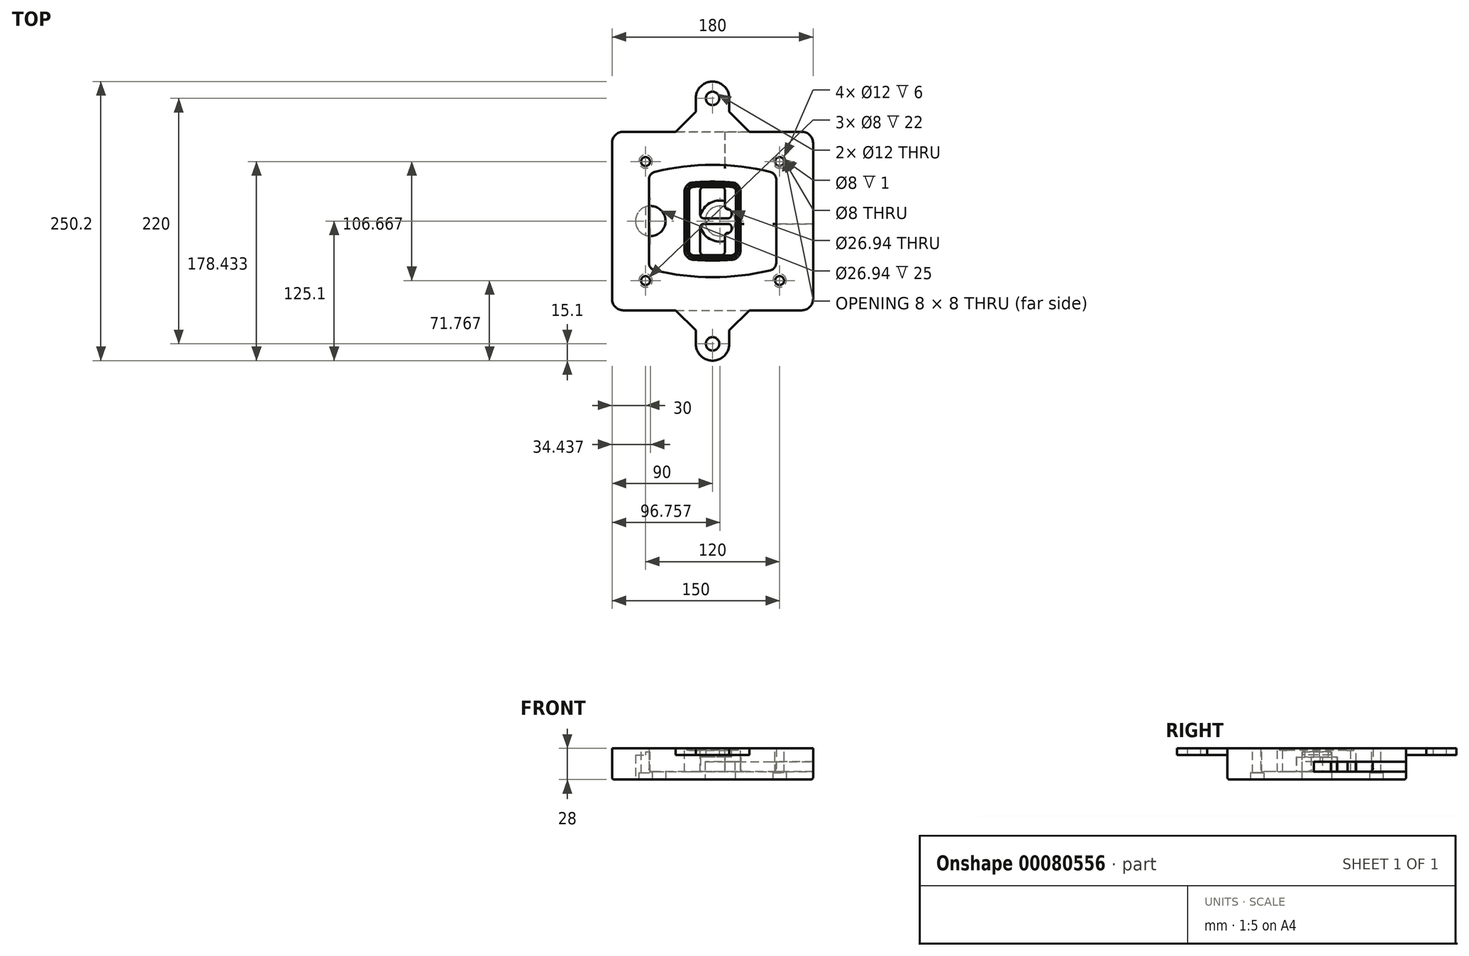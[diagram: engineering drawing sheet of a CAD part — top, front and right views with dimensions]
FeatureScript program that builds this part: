
annotation { "Feature Type Name" : "Feature", "Feature Type Description" : "" }
export const myFeature = defineFeature(function(context is Context, id is Id, definition is map)
    precondition{}
    {
        {
            var Q0;
            Q0=qCreatedBy(makeId("Top.planeOp"),FACE);
            var sketch = newSketch(context, id + "F0", { "sketchPlane" : qUnion([Q0])});
            skPoint(sketch, "E0.rect.middle", {"position": v(0, 0) * mm});
            skLineSegment(sketch, "E1.bottom", {"start": v(-80, -80) * mm, "end": v(80, -80) * mm});
            skLineSegment(sketch, "E1.top", {"start": v(-80, 80) * mm, "end": v(80, 80) * mm});
            skLineSegment(sketch, "E1.left", {"start": v(-90, -70) * mm, "end": v(-90, 70) * mm});
            skLineSegment(sketch, "E1.right", {"start": v(90, -70) * mm, "end": v(90, 70) * mm});
            skLineSegment(sketch, "E2", {"start": v(-90, 80) * mm, "end": v(90, -80) * mm, "construction": true});
            skLineSegment(sketch, "E3", {"start": v(90, 80) * mm, "end": v(-90, -80) * mm, "construction": true});
            skCircle(sketch, "E4", {"center": v(-60, 53.33) * mm, "radius": 4 * mm});
            skCircle(sketch, "E5", {"center": v(60, 53.33) * mm, "radius": 4 * mm});
            skCircle(sketch, "E6", {"center": v(60, -53.33) * mm, "radius": 4 * mm});
            skCircle(sketch, "E7", {"center": v(-60, -53.33) * mm, "radius": 4 * mm});
            skLineSegment(sketch, "E8", {"start": v(-60, 53.33) * mm, "end": v(60, 53.33) * mm, "construction": true});
            skLineSegment(sketch, "E9", {"start": v(60, 53.33) * mm, "end": v(60, -53.33) * mm, "construction": true});
            skLineSegment(sketch, "E10", {"start": v(60, -53.33) * mm, "end": v(-60, -53.33) * mm, "construction": true});
            skLineSegment(sketch, "E11", {"start": v(-60, -53.33) * mm, "end": v(-60, 53.33) * mm, "construction": true});
            skLineSegment(sketch, "E12", {"start": v(-60, 37.3) * mm, "end": v(-60, -37.3) * mm});
            skLineSegment(sketch, "E13", {"start": v(60, 37.3) * mm, "end": v(60, -37.3) * mm});
            skArc(sketch, "E14", {"start": v(52.38, 47.01) * mm, "mid": v(0, 53.33) * mm, "end": v(-52.38, 47.01) * mm});
            skArc(sketch, "E15", {"start": v(-52.38, -47.01) * mm, "mid": v(0, -53.33) * mm, "end": v(52.38, -47.01) * mm});
            skLineSegment(sketch, "E16", {"start": v(-60, 0) * mm, "end": v(60, 0) * mm, "construction": true});
            skPoint(sketch, "E17.visualSharp", {"position": v(-60, -45) * mm});
            skArc(sketch, "E17.filletArc", {"start": v(-60, -37.3) * mm, "mid": v(-57.87, -43.47) * mm, "end": v(-52.38, -47.01) * mm});
            skPoint(sketch, "E18.visualSharp", {"position": v(-60, 45) * mm});
            skArc(sketch, "E18.filletArc", {"start": v(-52.38, 47.01) * mm, "mid": v(-57.87, 43.47) * mm, "end": v(-60, 37.3) * mm});
            skPoint(sketch, "E19.visualSharp", {"position": v(60, 45) * mm});
            skArc(sketch, "E19.filletArc", {"start": v(60, 37.3) * mm, "mid": v(57.87, 43.47) * mm, "end": v(52.38, 47.01) * mm});
            skPoint(sketch, "E20.visualSharp", {"position": v(60, -45) * mm});
            skArc(sketch, "E20.filletArc", {"start": v(52.38, -47.01) * mm, "mid": v(57.87, -43.47) * mm, "end": v(60, -37.3) * mm});
            skPoint(sketch, "E21.visualSharp", {"position": v(-90, 80) * mm});
            skArc(sketch, "E21.filletArc", {"start": v(-80, 80) * mm, "mid": v(-87.07, 77.07) * mm, "end": v(-90, 70) * mm});
            skPoint(sketch, "E22.visualSharp", {"position": v(90, 80) * mm});
            skArc(sketch, "E22.filletArc", {"start": v(90, 70) * mm, "mid": v(87.07, 77.07) * mm, "end": v(80, 80) * mm});
            skPoint(sketch, "E23.visualSharp", {"position": v(90, -80) * mm});
            skArc(sketch, "E23.filletArc", {"start": v(80, -80) * mm, "mid": v(87.07, -77.07) * mm, "end": v(90, -70) * mm});
            skPoint(sketch, "E24.visualSharp", {"position": v(-90, -80) * mm});
            skArc(sketch, "E24.filletArc", {"start": v(-90, -70) * mm, "mid": v(-87.07, -77.07) * mm, "end": v(-80, -80) * mm});
            skArc(sketch, "E25.0", {"start": v(57, 37.3) * mm, "mid": v(55.5, 41.62) * mm, "end": v(51.67, 44.1) * mm});
            skLineSegment(sketch, "E25.1", {"start": v(57, 37.3) * mm, "end": v(57, -37.3) * mm});
            skArc(sketch, "E25.2", {"start": v(51.67, -44.1) * mm, "mid": v(55.5, -41.62) * mm, "end": v(57, -37.3) * mm});
            skArc(sketch, "E25.3", {"start": v(-51.67, -44.1) * mm, "mid": v(0, -50.33) * mm, "end": v(51.67, -44.1) * mm});
            skArc(sketch, "E25.4", {"start": v(-57, -37.3) * mm, "mid": v(-55.5, -41.62) * mm, "end": v(-51.67, -44.1) * mm});
            skArc(sketch, "E25.5", {"start": v(51.67, 44.1) * mm, "mid": v(0, 50.33) * mm, "end": v(-51.67, 44.1) * mm});
            skLineSegment(sketch, "E25.6", {"start": v(-57, 37.3) * mm, "end": v(-57, -37.3) * mm});
            skArc(sketch, "E25.7", {"start": v(-51.67, 44.1) * mm, "mid": v(-55.5, 41.62) * mm, "end": v(-57, 37.3) * mm});
            skArc(sketch, "E26.0", {"start": v(-53.33, 50.9) * mm, "mid": v(-61.01, 45.94) * mm, "end": v(-64, 37.3) * mm});
            skArc(sketch, "E26.1", {"start": v(53.33, 50.9) * mm, "mid": v(0, 57.33) * mm, "end": v(-53.33, 50.9) * mm});
            skArc(sketch, "E26.2", {"start": v(64, 37.3) * mm, "mid": v(61.01, 45.94) * mm, "end": v(53.33, 50.9) * mm});
            skLineSegment(sketch, "E26.3", {"start": v(64, 37.3) * mm, "end": v(64, -37.3) * mm});
            skArc(sketch, "E26.4", {"start": v(53.33, -50.9) * mm, "mid": v(61.01, -45.94) * mm, "end": v(64, -37.3) * mm});
            skLineSegment(sketch, "E26.5", {"start": v(-64, 37.3) * mm, "end": v(-64, -37.3) * mm});
            skArc(sketch, "E26.6", {"start": v(-53.33, -50.9) * mm, "mid": v(0, -57.33) * mm, "end": v(53.33, -50.9) * mm});
            skArc(sketch, "E26.7", {"start": v(-64, -37.3) * mm, "mid": v(-61.01, -45.94) * mm, "end": v(-53.33, -50.9) * mm});
            skSolve(sketch);
        }
        {
            var Q0;
            Q0=makeQuery(id+"F0.imprint","IMPRINT",FACE,{"disambiguationData":[TD([[makeQuery(id+"F0.imprint","IMPRINT",EDGE,{"derivedFrom":sQuery(id+"F0.wireOp",EDGE,"E1.bottom")}),1.0]])]});
            var Q1;
            Q1=makeQuery(id+"F0.imprint","IMPRINT",FACE,{"disambiguationData":[TD([[makeQuery(id+"F0.imprint","IMPRINT",EDGE,{"derivedFrom":sQuery(id+"F0.wireOp",EDGE,"E12")}),1.0]])]});
            var Q2;
            Q2=makeQuery(id+"F0.imprint","IMPRINT",FACE,{"disambiguationData":[TD([[makeQuery(id+"F0.imprint","IMPRINT",EDGE,{"derivedFrom":sQuery(id+"F0.wireOp",EDGE,"E25.0")}),1.0]])]});
            var Q3;
            Q3=makeQuery(id+"F0.imprint","IMPRINT",FACE,{"disambiguationData":[TD([[makeQuery(id+"F0.imprint","IMPRINT",EDGE,{"derivedFrom":sQuery(id+"F0.wireOp",EDGE,"E12")}),-1.0]])]});
            extrude(context, id + "F1", {"entities" : qUnion([Q0, Q1, Q2, Q3]), "oppositeDirection" : true, "depth" : 25 * mm});
        }
        {
            var Q0;
            Q0=makeQuery(id+"F0.imprint","IMPRINT",FACE,{"disambiguationData":[TD([[makeQuery(id+"F0.imprint","IMPRINT",EDGE,{"derivedFrom":sQuery(id+"F0.wireOp",EDGE,"E12")}),1.0]])]});
            extrude(context, id + "F2", {"entities" : qUnion([Q0]), "operationType" : NewBodyOperationType.ADD, "depth" : 3 * mm});
        }
        {
            var Q0;
            Q0=makeQuery(id+"F0.imprint","IMPRINT",FACE,{"disambiguationData":[TD([[makeQuery(id+"F0.imprint","IMPRINT",EDGE,{"derivedFrom":sQuery(id+"F0.wireOp",EDGE,"E25.0")}),1.0]])]});
            extrude(context, id + "F3", {"entities" : qUnion([Q0]), "operationType" : NewBodyOperationType.REMOVE, "oppositeDirection" : true, "depth" : 18 * mm});
        }
        {
            var Q0;
            Q0=makeQuery(id+"F2.opExtrude","CAP_FACE",FACE,{"disambiguationData":[OSD([sQuery(id+"F0.wireOp",EDGE,"E12"),sQuery(id+"F0.wireOp",EDGE,"E13"),sQuery(id+"F0.wireOp",EDGE,"E14"),sQuery(id+"F0.wireOp",EDGE,"E15"),sQuery(id+"F0.wireOp",EDGE,"E17.filletArc"),sQuery(id+"F0.wireOp",EDGE,"E18.filletArc"),sQuery(id+"F0.wireOp",EDGE,"E19.filletArc"),sQuery(id+"F0.wireOp",EDGE,"E20.filletArc"),sQuery(id+"F0.wireOp",EDGE,"E25.0"),sQuery(id+"F0.wireOp",EDGE,"E25.1"),sQuery(id+"F0.wireOp",EDGE,"E25.2"),sQuery(id+"F0.wireOp",EDGE,"E25.3"),sQuery(id+"F0.wireOp",EDGE,"E25.4"),sQuery(id+"F0.wireOp",EDGE,"E25.5"),sQuery(id+"F0.wireOp",EDGE,"E25.6"),sQuery(id+"F0.wireOp",EDGE,"E25.7")])],"isStart":false});
            var sketch = newSketch(context, id + "F4", { "sketchPlane" : qUnion([Q0])});
            skArc(sketch, "E27.0", {"start": v(-17.7, -34.56) * mm, "mid": v(0, -35.33) * mm, "end": v(17.7, -34.56) * mm});
            skArc(sketch, "E28.0", {"start": v(17.7, 34.56) * mm, "mid": v(0, 35.33) * mm, "end": v(-17.7, 34.56) * mm});
            skLineSegment(sketch, "E29", {"start": v(-25, 26.59) * mm, "end": v(-25, -26.59) * mm});
            skLineSegment(sketch, "E30", {"start": v(25, 26.59) * mm, "end": v(25, -26.59) * mm});
            skLineSegment(sketch, "E31", {"start": v(-25, 33.78) * mm, "end": v(25, 33.78) * mm, "construction": true});
            skLineSegment(sketch, "E32", {"start": v(-25, -33.78) * mm, "end": v(25, -33.78) * mm, "construction": true});
            skPoint(sketch, "E33.visualSharp", {"position": v(-25, 33.78) * mm});
            skArc(sketch, "E33.filletArc", {"start": v(-17.7, 34.56) * mm, "mid": v(-22.9, 32) * mm, "end": v(-25, 26.59) * mm});
            skPoint(sketch, "E34.visualSharp", {"position": v(25, 33.78) * mm});
            skArc(sketch, "E34.filletArc", {"start": v(25, 26.59) * mm, "mid": v(22.9, 32) * mm, "end": v(17.7, 34.56) * mm});
            skPoint(sketch, "E35.visualSharp", {"position": v(25, -33.78) * mm});
            skArc(sketch, "E35.filletArc", {"start": v(17.7, -34.56) * mm, "mid": v(22.9, -32) * mm, "end": v(25, -26.59) * mm});
            skPoint(sketch, "E36.visualSharp", {"position": v(-25, -33.78) * mm});
            skArc(sketch, "E36.filletArc", {"start": v(-25, -26.59) * mm, "mid": v(-22.9, -32) * mm, "end": v(-17.7, -34.56) * mm});
            skArc(sketch, "E37.0", {"start": v(51.67, 44.1) * mm, "mid": v(0, 50.33) * mm, "end": v(-51.67, 44.1) * mm});
            skArc(sketch, "E37.1", {"start": v(-51.67, 44.1) * mm, "mid": v(-55.5, 41.62) * mm, "end": v(-57, 37.3) * mm});
            skLineSegment(sketch, "E37.2", {"start": v(-57, 37.3) * mm, "end": v(-57, -37.3) * mm});
            skArc(sketch, "E37.3", {"start": v(-57, -37.3) * mm, "mid": v(-55.5, -41.62) * mm, "end": v(-51.67, -44.1) * mm});
            skArc(sketch, "E37.4", {"start": v(-51.67, -44.1) * mm, "mid": v(0, -50.33) * mm, "end": v(51.67, -44.1) * mm});
            skArc(sketch, "E37.5", {"start": v(51.67, -44.1) * mm, "mid": v(55.5, -41.62) * mm, "end": v(57, -37.3) * mm});
            skLineSegment(sketch, "E37.6", {"start": v(57, 37.3) * mm, "end": v(57, -37.3) * mm});
            skArc(sketch, "E37.7", {"start": v(57, 37.3) * mm, "mid": v(55.5, 41.62) * mm, "end": v(51.67, 44.1) * mm});
            skLineSegment(sketch, "E38.0", {"start": v(23, 26.59) * mm, "end": v(23, -26.59) * mm});
            skArc(sketch, "E38.1", {"start": v(17.53, -32.56) * mm, "mid": v(21.42, -30.64) * mm, "end": v(23, -26.59) * mm});
            skArc(sketch, "E38.2", {"start": v(-17.53, -32.56) * mm, "mid": v(0, -33.33) * mm, "end": v(17.53, -32.56) * mm});
            skArc(sketch, "E38.3", {"start": v(-23, -26.59) * mm, "mid": v(-21.42, -30.64) * mm, "end": v(-17.53, -32.56) * mm});
            skLineSegment(sketch, "E38.4", {"start": v(-23, 26.59) * mm, "end": v(-23, -26.59) * mm});
            skArc(sketch, "E38.5", {"start": v(23, 26.59) * mm, "mid": v(21.42, 30.64) * mm, "end": v(17.53, 32.56) * mm});
            skArc(sketch, "E38.6", {"start": v(-17.53, 32.56) * mm, "mid": v(-21.42, 30.64) * mm, "end": v(-23, 26.59) * mm});
            skArc(sketch, "E38.7", {"start": v(17.53, 32.56) * mm, "mid": v(0, 33.33) * mm, "end": v(-17.53, 32.56) * mm});
            skArc(sketch, "E39.0", {"start": v(21, 26.59) * mm, "mid": v(19.95, 29.29) * mm, "end": v(17.35, 30.57) * mm});
            skLineSegment(sketch, "E39.1", {"start": v(21, 26.59) * mm, "end": v(21, -26.59) * mm});
            skArc(sketch, "E39.2", {"start": v(17.35, -30.57) * mm, "mid": v(19.95, -29.29) * mm, "end": v(21, -26.59) * mm});
            skArc(sketch, "E39.3", {"start": v(-17.35, -30.57) * mm, "mid": v(0, -31.33) * mm, "end": v(17.35, -30.57) * mm});
            skArc(sketch, "E39.4", {"start": v(-21, -26.59) * mm, "mid": v(-19.95, -29.29) * mm, "end": v(-17.35, -30.57) * mm});
            skArc(sketch, "E39.5", {"start": v(17.35, 30.57) * mm, "mid": v(0, 31.33) * mm, "end": v(-17.35, 30.57) * mm});
            skLineSegment(sketch, "E39.6", {"start": v(-21, 26.59) * mm, "end": v(-21, -26.59) * mm});
            skArc(sketch, "E39.7", {"start": v(-17.35, 30.57) * mm, "mid": v(-19.95, 29.29) * mm, "end": v(-21, 26.59) * mm});
            skLineSegment(sketch, "E40", {"start": v(-25, 0) * mm, "end": v(25, 0) * mm, "construction": true});
            skLineSegment(sketch, "E41", {"start": v(-11, 5.5) * mm, "end": v(-11, 27.5) * mm});
            skLineSegment(sketch, "E42", {"start": v(-8, 30.5) * mm, "end": v(8, 30.5) * mm});
            skLineSegment(sketch, "E43", {"start": v(11, 27.5) * mm, "end": v(11, 13.5) * mm});
            skLineSegment(sketch, "E44", {"start": v(14, 10.5) * mm, "end": v(14, 10.5) * mm});
            skLineSegment(sketch, "E45", {"start": v(17, 7.5) * mm, "end": v(17, 5.5) * mm});
            skLineSegment(sketch, "E46", {"start": v(14, 2.5) * mm, "end": v(-8, 2.5) * mm});
            skPoint(sketch, "E47.visualSharp", {"position": v(-11, 30.5) * mm});
            skArc(sketch, "E47.filletArc", {"start": v(-8, 30.5) * mm, "mid": v(-10.12, 29.62) * mm, "end": v(-11, 27.5) * mm});
            skPoint(sketch, "E48.visualSharp", {"position": v(11, 30.5) * mm});
            skArc(sketch, "E48.filletArc", {"start": v(11, 27.5) * mm, "mid": v(10.12, 29.62) * mm, "end": v(8, 30.5) * mm});
            skPoint(sketch, "E49.visualSharp", {"position": v(11, 10.5) * mm});
            skArc(sketch, "E49.filletArc", {"start": v(11, 13.5) * mm, "mid": v(11.88, 11.38) * mm, "end": v(14, 10.5) * mm});
            skPoint(sketch, "E50.visualSharp", {"position": v(17, 10.5) * mm});
            skArc(sketch, "E50.filletArc", {"start": v(17, 7.5) * mm, "mid": v(16.12, 9.62) * mm, "end": v(14, 10.5) * mm});
            skPoint(sketch, "E51.visualSharp", {"position": v(17, 2.5) * mm});
            skArc(sketch, "E51.filletArc", {"start": v(14, 2.5) * mm, "mid": v(16.12, 3.38) * mm, "end": v(17, 5.5) * mm});
            skPoint(sketch, "E52.visualSharp", {"position": v(-11, 2.5) * mm});
            skArc(sketch, "E52.filletArc", {"start": v(-11, 5.5) * mm, "mid": v(-10.12, 3.38) * mm, "end": v(-8, 2.5) * mm});
            skLineSegment(sketch, "E53.0.MirrorCS", {"start": v(14, -2.5) * mm, "end": v(-8, -2.5) * mm});
            skArc(sketch, "E54.0.MirrorCS", {"start": v(-11, -5.5) * mm, "mid": v(-10.12, -3.38) * mm, "end": v(-8, -2.5) * mm});
            skLineSegment(sketch, "E55.0.MirrorCS", {"start": v(-11, -5.5) * mm, "end": v(-11, -27.5) * mm});
            skArc(sketch, "E56.0.MirrorCS", {"start": v(-8, -30.5) * mm, "mid": v(-10.12, -29.62) * mm, "end": v(-11, -27.5) * mm});
            skLineSegment(sketch, "E57.0.MirrorCS", {"start": v(-8, -30.5) * mm, "end": v(8, -30.5) * mm});
            skArc(sketch, "E58.0.MirrorCS", {"start": v(11, -27.5) * mm, "mid": v(10.12, -29.62) * mm, "end": v(8, -30.5) * mm});
            skLineSegment(sketch, "E59.0.MirrorCS", {"start": v(11, -27.5) * mm, "end": v(11, -13.5) * mm});
            skArc(sketch, "E60.0.MirrorCS", {"start": v(11, -13.5) * mm, "mid": v(11.88, -11.38) * mm, "end": v(14, -10.5) * mm});
            skArc(sketch, "E61.0.MirrorCS", {"start": v(17, -7.5) * mm, "mid": v(16.12, -9.62) * mm, "end": v(14, -10.5) * mm});
            skLineSegment(sketch, "E62.0.MirrorCS", {"start": v(17, -7.5) * mm, "end": v(17, -5.5) * mm});
            skArc(sketch, "E63.0.MirrorCS", {"start": v(14, -2.5) * mm, "mid": v(16.12, -3.38) * mm, "end": v(17, -5.5) * mm});
            skSolve(sketch);
        }
        {
            var Q0;
            Q0=makeQuery(id+"F4.imprint","IMPRINT",FACE,{"disambiguationData":[TD([[makeQuery(id+"F4.imprint","IMPRINT",EDGE,{"derivedFrom":sQuery(id+"F4.wireOp",EDGE,"E27.0")}),1.0]])]});
            var Q1;
            Q1=makeQuery(id+"F4.imprint","IMPRINT",FACE,{"disambiguationData":[TD([[makeQuery(id+"F4.imprint","IMPRINT",EDGE,{"derivedFrom":sQuery(id+"F4.wireOp",EDGE,"E38.0")}),-1.0]])]});
            var Q2;
            Q2=makeQuery(id+"F4.imprint","IMPRINT",FACE,{"disambiguationData":[TD([[makeQuery(id+"F4.imprint","IMPRINT",EDGE,{"derivedFrom":sQuery(id+"F4.wireOp",EDGE,"E39.0")}),1.0]])]});
            extrude(context, id + "F5", {"entities" : qUnion([Q0, Q1, Q2]), "operationType" : NewBodyOperationType.ADD, "endBound" : BoundingType.UP_TO_NEXT, "oppositeDirection" : true, "depth" : 25 * mm});
        }
        {
            var Q0;
            Q0=makeQuery(id+"F4.imprint","IMPRINT",FACE,{"disambiguationData":[TD([[makeQuery(id+"F4.imprint","IMPRINT",EDGE,{"derivedFrom":sQuery(id+"F4.wireOp",EDGE,"E38.0")}),-1.0]])]});
            extrude(context, id + "F6", {"entities" : qUnion([Q0]), "operationType" : NewBodyOperationType.REMOVE, "oppositeDirection" : true, "depth" : 2 * mm});
        }
        {
            var Q0;
            Q0=makeQuery(id+"F1.opExtrude","CAP_FACE",FACE,{"disambiguationData":[OSD([sQuery(id+"F0.wireOp",EDGE,"E1.bottom"),sQuery(id+"F0.wireOp",EDGE,"E1.top"),sQuery(id+"F0.wireOp",EDGE,"E1.left"),sQuery(id+"F0.wireOp",EDGE,"E1.right"),sQuery(id+"F0.wireOp",EDGE,"E4"),sQuery(id+"F0.wireOp",EDGE,"E5"),sQuery(id+"F0.wireOp",EDGE,"E6"),sQuery(id+"F0.wireOp",EDGE,"E7"),sQuery(id+"F0.wireOp",EDGE,"E21.filletArc"),sQuery(id+"F0.wireOp",EDGE,"E22.filletArc"),sQuery(id+"F0.wireOp",EDGE,"E23.filletArc"),sQuery(id+"F0.wireOp",EDGE,"E24.filletArc")])],"isStart":false});
            var sketch = newSketch(context, id + "F7", { "sketchPlane" : qUnion([Q0])});
            skCircle(sketch, "E64", {"center": v(6.76, 0) * mm, "radius": 13.47 * mm});
            skCircle(sketch, "E65", {"center": v(-55.56, 0) * mm, "radius": 13.47 * mm});
            skLineSegment(sketch, "E66", {"start": v(90, 0) * mm, "end": v(-90, 0) * mm});
            skCircle(sketch, "E67", {"center": v(6.76, 0) * mm, "radius": 18.47 * mm});
            skCircle(sketch, "E68", {"center": v(60, -53.33) * mm, "radius": 6 * mm});
            skCircle(sketch, "E69", {"center": v(-60, -53.33) * mm, "radius": 6 * mm});
            skCircle(sketch, "E70", {"center": v(-60, 53.33) * mm, "radius": 6 * mm});
            skCircle(sketch, "E71", {"center": v(60, 53.33) * mm, "radius": 6 * mm});
            skSolve(sketch);
        }
        {
            var Q0;
            {var subQ1=sQuery(id+"F7.wireOp",EDGE,"E66");var subQ4=sQuery(id+"F7.wireOp",EDGE,"E64");var subQ6=makeQuery(id+"F7.imprint","INTERSECT",VERTEX,{"disambiguationData":[OD(0.0)],"derivedFrom":[subQ4,subQ1]});Q0=makeQuery(id+"F7.imprint","IMPRINT",FACE,{"disambiguationData":[TD([[makeQuery(id+"F7.imprint","IMPRINT",EDGE,{"disambiguationData":[TD([[subQ6,-1.0]])],"derivedFrom":subQ4}),-1.0]])]});}
            var Q1;
            {var subQ0=sQuery(id+"F7.wireOp",EDGE,"E66");var subQ1=sQuery(id+"F7.wireOp",EDGE,"E64");var subQ3=makeQuery(id+"F7.imprint","INTERSECT",VERTEX,{"disambiguationData":[OD(0.0)],"derivedFrom":[subQ1,subQ0]});Q1=makeQuery(id+"F7.imprint","IMPRINT",FACE,{"disambiguationData":[TD([[makeQuery(id+"F7.imprint","IMPRINT",EDGE,{"disambiguationData":[TD([[subQ3,-1.0]])],"derivedFrom":subQ1}),1.0]])]});}
            var Q2;
            {var subQ0=sQuery(id+"F7.wireOp",EDGE,"E66");var subQ1=sQuery(id+"F7.wireOp",EDGE,"E64");var subQ3=makeQuery(id+"F7.imprint","INTERSECT",VERTEX,{"disambiguationData":[OD(0.0)],"derivedFrom":[subQ1,subQ0]});Q2=makeQuery(id+"F7.imprint","IMPRINT",FACE,{"disambiguationData":[TD([[makeQuery(id+"F7.imprint","IMPRINT",EDGE,{"disambiguationData":[TD([[subQ3,1.0]])],"derivedFrom":subQ1}),1.0]])]});}
            var Q3;
            {var subQ1=sQuery(id+"F7.wireOp",EDGE,"E66");var subQ4=sQuery(id+"F7.wireOp",EDGE,"E64");var subQ6=makeQuery(id+"F7.imprint","INTERSECT",VERTEX,{"disambiguationData":[OD(0.0)],"derivedFrom":[subQ4,subQ1]});Q3=makeQuery(id+"F7.imprint","IMPRINT",FACE,{"disambiguationData":[TD([[makeQuery(id+"F7.imprint","IMPRINT",EDGE,{"disambiguationData":[TD([[subQ6,1.0]])],"derivedFrom":subQ4}),-1.0]])]});}
            extrude(context, id + "F8", {"entities" : qUnion([Q0, Q1, Q2, Q3]), "operationType" : NewBodyOperationType.ADD, "oppositeDirection" : true, "depth" : 20 * mm});
        }
        {
            var Q0;
            {var subQ0=sQuery(id+"F7.wireOp",EDGE,"E66");var subQ1=sQuery(id+"F7.wireOp",EDGE,"E64");var subQ3=makeQuery(id+"F7.imprint","INTERSECT",VERTEX,{"disambiguationData":[OD(0.0)],"derivedFrom":[subQ1,subQ0]});Q0=makeQuery(id+"F7.imprint","IMPRINT",FACE,{"disambiguationData":[TD([[makeQuery(id+"F7.imprint","IMPRINT",EDGE,{"disambiguationData":[TD([[subQ3,-1.0]])],"derivedFrom":subQ1}),1.0]])]});}
            var Q1;
            {var subQ0=sQuery(id+"F7.wireOp",EDGE,"E66");var subQ1=sQuery(id+"F7.wireOp",EDGE,"E64");var subQ3=makeQuery(id+"F7.imprint","INTERSECT",VERTEX,{"disambiguationData":[OD(0.0)],"derivedFrom":[subQ1,subQ0]});Q1=makeQuery(id+"F7.imprint","IMPRINT",FACE,{"disambiguationData":[TD([[makeQuery(id+"F7.imprint","IMPRINT",EDGE,{"disambiguationData":[TD([[subQ3,1.0]])],"derivedFrom":subQ1}),1.0]])]});}
            extrude(context, id + "F9", {"entities" : qUnion([Q0, Q1]), "operationType" : NewBodyOperationType.REMOVE, "oppositeDirection" : true, "depth" : 16 * mm});
        }
        {
            var Q0;
            {var subQ0=sQuery(id+"F7.wireOp",EDGE,"E66");var subQ1=sQuery(id+"F7.wireOp",EDGE,"E65");var subQ3=makeQuery(id+"F7.imprint","INTERSECT",VERTEX,{"disambiguationData":[OD(0.0)],"derivedFrom":[subQ1,subQ0]});Q0=makeQuery(id+"F7.imprint","IMPRINT",FACE,{"disambiguationData":[TD([[makeQuery(id+"F7.imprint","IMPRINT",EDGE,{"disambiguationData":[TD([[subQ3,-1.0]])],"derivedFrom":subQ1}),1.0]])]});}
            var Q1;
            {var subQ0=sQuery(id+"F7.wireOp",EDGE,"E66");var subQ1=sQuery(id+"F7.wireOp",EDGE,"E65");var subQ3=makeQuery(id+"F7.imprint","INTERSECT",VERTEX,{"disambiguationData":[OD(0.0)],"derivedFrom":[subQ1,subQ0]});Q1=makeQuery(id+"F7.imprint","IMPRINT",FACE,{"disambiguationData":[TD([[makeQuery(id+"F7.imprint","IMPRINT",EDGE,{"disambiguationData":[TD([[subQ3,1.0]])],"derivedFrom":subQ1}),1.0]])]});}
            extrude(context, id + "F10", {"entities" : qUnion([Q0, Q1]), "operationType" : NewBodyOperationType.REMOVE, "oppositeDirection" : true, "depth" : 25 * mm});
        }
        {
            var Q0;
            Q0=makeQuery(id+"F7.imprint","IMPRINT",FACE,{"disambiguationData":[TD([[makeQuery(id+"F7.imprint","IMPRINT",EDGE,{"derivedFrom":sQuery(id+"F7.wireOp",EDGE,"E68")}),1.0]])]});
            var Q1;
            Q1=makeQuery(id+"F7.imprint","IMPRINT",FACE,{"disambiguationData":[TD([[makeQuery(id+"F7.imprint","IMPRINT",EDGE,{"derivedFrom":makeQuery(id+"F1.opExtrude","CAP_EDGE",EDGE,{"disambiguationData":[OSD([sQuery(id+"F0.wireOp",EDGE,"E5")])],"isStart":false})}),-1.0]])]});
            var Q2;
            Q2=makeQuery(id+"F7.imprint","IMPRINT",FACE,{"disambiguationData":[TD([[makeQuery(id+"F7.imprint","IMPRINT",EDGE,{"derivedFrom":sQuery(id+"F7.wireOp",EDGE,"E69")}),1.0]])]});
            var Q3;
            Q3=makeQuery(id+"F7.imprint","IMPRINT",FACE,{"disambiguationData":[TD([[makeQuery(id+"F7.imprint","IMPRINT",EDGE,{"derivedFrom":makeQuery(id+"F1.opExtrude","CAP_EDGE",EDGE,{"disambiguationData":[OSD([sQuery(id+"F0.wireOp",EDGE,"E4")])],"isStart":false})}),-1.0]])]});
            var Q4;
            Q4=makeQuery(id+"F7.imprint","IMPRINT",FACE,{"disambiguationData":[TD([[makeQuery(id+"F7.imprint","IMPRINT",EDGE,{"derivedFrom":sQuery(id+"F7.wireOp",EDGE,"E70")}),1.0]])]});
            var Q5;
            Q5=makeQuery(id+"F7.imprint","IMPRINT",FACE,{"disambiguationData":[TD([[makeQuery(id+"F7.imprint","IMPRINT",EDGE,{"derivedFrom":makeQuery(id+"F1.opExtrude","CAP_EDGE",EDGE,{"disambiguationData":[OSD([sQuery(id+"F0.wireOp",EDGE,"E7")])],"isStart":false})}),-1.0]])]});
            var Q6;
            Q6=makeQuery(id+"F7.imprint","IMPRINT",FACE,{"disambiguationData":[TD([[makeQuery(id+"F7.imprint","IMPRINT",EDGE,{"derivedFrom":sQuery(id+"F7.wireOp",EDGE,"E71")}),1.0]])]});
            var Q7;
            Q7=makeQuery(id+"F7.imprint","IMPRINT",FACE,{"disambiguationData":[TD([[makeQuery(id+"F7.imprint","IMPRINT",EDGE,{"derivedFrom":makeQuery(id+"F1.opExtrude","CAP_EDGE",EDGE,{"disambiguationData":[OSD([sQuery(id+"F0.wireOp",EDGE,"E6")])],"isStart":false})}),-1.0]])]});
            extrude(context, id + "F11", {"entities" : qUnion([Q0, Q1, Q2, Q3, Q4, Q5, Q6, Q7]), "operationType" : NewBodyOperationType.REMOVE, "oppositeDirection" : true, "depth" : 6 * mm});
        }
        {
            var Q0;
            Q0=makeQuery(id+"F9.boolean.opBoolean","COPY",FACE,{"derivedFrom":makeQuery(id+"F9.opExtrude","CAP_FACE",FACE,{"disambiguationData":[OSD([sQuery(id+"F7.wireOp",EDGE,"E64")])],"isStart":false})});
            var sketch = newSketch(context, id + "F12", { "sketchPlane" : qUnion([Q0])});
            skArc(sketch, "E72.0", {"start": v(11, -88.19) * mm, "mid": v(97.1, -83.6) * mm, "end": v(92.5, 2.5) * mm});
            skLineSegment(sketch, "E72.1", {"start": v(11, -17.97) * mm, "end": v(11, -17.97) * mm});
            skLineSegment(sketch, "E73", {"start": v(92.5, -105.13) * mm, "end": v(102.3, -105.13) * mm});
            skLineSegment(sketch, "E74.0", {"start": v(92.5, 2.5) * mm, "end": v(14, 2.5) * mm});
            skArc(sketch, "E74.1", {"start": v(14, 2.5) * mm, "mid": v(16.12, 3.38) * mm, "end": v(17, 5.5) * mm});
            skLineSegment(sketch, "E74.2", {"start": v(17, 7.5) * mm, "end": v(17, 5.5) * mm});
            skArc(sketch, "E74.3", {"start": v(17, 7.5) * mm, "mid": v(16.12, 9.62) * mm, "end": v(14, 10.5) * mm});
            skArc(sketch, "E74.4", {"start": v(11, 13.5) * mm, "mid": v(11.88, 11.38) * mm, "end": v(14, 10.5) * mm});
            skLineSegment(sketch, "E74.5", {"start": v(11, 13.5) * mm, "end": v(11, -88.19) * mm});
            skLineSegment(sketch, "E74.7", {"start": v(92.5, -2.5) * mm, "end": v(14, -2.5) * mm});
            skArc(sketch, "E74.8", {"start": v(14, -2.5) * mm, "mid": v(16.12, -3.38) * mm, "end": v(17, -5.5) * mm});
            skLineSegment(sketch, "E74.9", {"start": v(17, -7.5) * mm, "end": v(17, -5.5) * mm});
            skArc(sketch, "E74.10", {"start": v(17, -7.5) * mm, "mid": v(16.12, -9.62) * mm, "end": v(14, -10.5) * mm});
            skArc(sketch, "E74.11", {"start": v(11, -13.5) * mm, "mid": v(11.88, -11.38) * mm, "end": v(14, -10.5) * mm});
            skLineSegment(sketch, "E74.12", {"start": v(11, -17.97) * mm, "end": v(11, -13.5) * mm});
            skPoint(sketch, "E75.orphan", {"position": v(11, -27.5) * mm});
            skPoint(sketch, "E76.orphan", {"position": v(-8, -2.5) * mm});
            skPoint(sketch, "E77.orphan", {"position": v(-8, 2.5) * mm});
            skPoint(sketch, "E78.orphan", {"position": v(11, 27.5) * mm});
            skSolve(sketch);
        }
        {
            var Q0;
            {var subQ7=sQuery(id+"F12.wireOp",EDGE,"E72.0");var subQ14=sQuery(id+"F12.wireOp",EDGE,"E72.1");var subQ16=sQuery(id+"F12.wireOp",EDGE,"E74.1");var subQ18=sQuery(id+"F12.wireOp",EDGE,"E74.8");Q0=qUnion([makeQuery(id+"F12.imprint","IMPRINT",FACE,{"disambiguationData":[TD([[makeQuery(id+"F12.imprint","IMPRINT",EDGE,{"derivedFrom":subQ7}),1.0]])]}),makeQuery(id+"F12.imprint","IMPRINT",FACE,{"disambiguationData":[TD([[makeQuery(id+"F12.imprint","IMPRINT",EDGE,{"derivedFrom":subQ14}),1.0]])]}),makeQuery(id+"F12.imprint","IMPRINT",FACE,{"disambiguationData":[TD([[makeQuery(id+"F12.imprint","IMPRINT",EDGE,{"derivedFrom":subQ16}),1.0]])]}),makeQuery(id+"F12.imprint","IMPRINT",FACE,{"disambiguationData":[TD([[makeQuery(id+"F12.imprint","IMPRINT",EDGE,{"derivedFrom":subQ18}),-1.0]])]})]);}
            var Q1;
            Q1=makeQuery(id+"F5.boolean.opBoolean","SPLIT",FACE,{"disambiguationData":[TD([makeQuery(id+"F5.opExtrude","SWEPT_FACE",FACE,{"disambiguationData":[OSD([sQuery(id+"F4.wireOp",EDGE,"E41")])]})])],"derivedFrom":makeQuery(id+"F3.boolean.opBoolean","COPY",FACE,{"derivedFrom":makeQuery(id+"F3.opExtrude","CAP_FACE",FACE,{"disambiguationData":[OSD([sQuery(id+"F0.wireOp",EDGE,"E25.0"),sQuery(id+"F0.wireOp",EDGE,"E25.1"),sQuery(id+"F0.wireOp",EDGE,"E25.2"),sQuery(id+"F0.wireOp",EDGE,"E25.3"),sQuery(id+"F0.wireOp",EDGE,"E25.4"),sQuery(id+"F0.wireOp",EDGE,"E25.5"),sQuery(id+"F0.wireOp",EDGE,"E25.6"),sQuery(id+"F0.wireOp",EDGE,"E25.7")])],"isStart":false})})});
            extrude(context, id + "F13", {"entities" : qUnion([Q0]), "operationType" : NewBodyOperationType.REMOVE, "endBound" : BoundingType.UP_TO_SURFACE, "endBoundEntityFace" : qUnion([Q1]), "depth" : 25 * mm});
        }
        {
            var Q0;
            Q0=makeQuery(id+"F3.boolean.opBoolean","COPY",EDGE,{"derivedFrom":makeQuery(id+"F3.opExtrude","CAP_EDGE",EDGE,{"disambiguationData":[OSD([sQuery(id+"F0.wireOp",EDGE,"E25.6")])],"isStart":false})});
            var Q1;
            Q1=makeQuery(id+"F8.boolean.opBoolean","INTERSECT",EDGE,{"derivedFrom":[makeQuery(id+"F5.opExtrude","SWEPT_FACE",FACE,{"disambiguationData":[OSD([sQuery(id+"F4.wireOp",EDGE,"E30")])]}),makeQuery(id+"F8.opExtrude","CAP_FACE",FACE,{"disambiguationData":[OSD([sQuery(id+"F7.wireOp",EDGE,"E67")])],"isStart":false})]});
            var Q2;
            Q2=makeQuery(id+"F8.boolean.opBoolean","INTERSECT",EDGE,{"disambiguationData":[OD(1.0)],"derivedFrom":[makeQuery(id+"F5.opExtrude","SWEPT_FACE",FACE,{"disambiguationData":[OSD([sQuery(id+"F4.wireOp",EDGE,"E30")])]}),makeQuery(id+"F8.opExtrude","SWEPT_FACE",FACE,{"disambiguationData":[OSD([sQuery(id+"F7.wireOp",EDGE,"E67")])]})]});
            var Q3;
            {var subQ0=makeQuery(id+"F3.boolean.opBoolean","COPY",FACE,{"derivedFrom":makeQuery(id+"F3.opExtrude","CAP_FACE",FACE,{"disambiguationData":[OSD([sQuery(id+"F0.wireOp",EDGE,"E25.0"),sQuery(id+"F0.wireOp",EDGE,"E25.1"),sQuery(id+"F0.wireOp",EDGE,"E25.2"),sQuery(id+"F0.wireOp",EDGE,"E25.3"),sQuery(id+"F0.wireOp",EDGE,"E25.4"),sQuery(id+"F0.wireOp",EDGE,"E25.5"),sQuery(id+"F0.wireOp",EDGE,"E25.6"),sQuery(id+"F0.wireOp",EDGE,"E25.7")])],"isStart":false})});var subQ1=sQuery(id+"F4.wireOp",EDGE,"E30");Q3=makeQuery(id+"F8.boolean.opBoolean","SPLIT",EDGE,{"disambiguationData":[TD([makeQuery(id+"F5.opExtrude","SWEPT_FACE",FACE,{"disambiguationData":[OSD([sQuery(id+"F4.wireOp",EDGE,"E35.filletArc")])]})])],"derivedFrom":makeQuery(id+"F5.opExtrude","TWEAK_EDGE",EDGE,{"derivedFrom":[subQ0,makeQuery(id+"F4.imprint","IMPRINT",EDGE,{"derivedFrom":subQ1})]})});}
            var Q4;
            {var subQ0=sQuery(id+"F0.wireOp",EDGE,"E25.0");var subQ1=sQuery(id+"F0.wireOp",EDGE,"E25.1");var subQ2=sQuery(id+"F0.wireOp",EDGE,"E25.2");var subQ3=sQuery(id+"F0.wireOp",EDGE,"E25.3");var subQ4=sQuery(id+"F0.wireOp",EDGE,"E25.4");var subQ5=sQuery(id+"F0.wireOp",EDGE,"E25.5");var subQ6=sQuery(id+"F0.wireOp",EDGE,"E25.6");var subQ7=sQuery(id+"F0.wireOp",EDGE,"E25.7");Q4=makeQuery(id+"F8.boolean.opBoolean","INTERSECT",EDGE,{"derivedFrom":[makeQuery(id+"F5.boolean.opBoolean","SPLIT",FACE,{"disambiguationData":[TD([makeQuery(id+"F2.opExtrude","SWEPT_FACE",FACE,{"disambiguationData":[OSD([subQ0])]})])],"derivedFrom":makeQuery(id+"F3.boolean.opBoolean","COPY",FACE,{"derivedFrom":makeQuery(id+"F3.opExtrude","CAP_FACE",FACE,{"disambiguationData":[OSD([subQ0,subQ1,subQ2,subQ3,subQ4,subQ5,subQ6,subQ7])],"isStart":false})})}),makeQuery(id+"F8.opExtrude","SWEPT_FACE",FACE,{"disambiguationData":[OSD([sQuery(id+"F7.wireOp",EDGE,"E67")])]})]});}
            var Q5;
            Q5=makeQuery(id+"F8.boolean.opBoolean","INTERSECT",EDGE,{"disambiguationData":[OD(0.0)],"derivedFrom":[makeQuery(id+"F5.opExtrude","SWEPT_FACE",FACE,{"disambiguationData":[OSD([sQuery(id+"F4.wireOp",EDGE,"E30")])]}),makeQuery(id+"F8.opExtrude","SWEPT_FACE",FACE,{"disambiguationData":[OSD([sQuery(id+"F7.wireOp",EDGE,"E67")])]})]});
            fillet(context, id + "F14", {"entities" : qUnion([Q0, Q1, Q2, Q3, Q4, Q5]), "radius" : 3 * mm, "tangentPropagation" : true, "allowEdgeOverflow" : false});
        }
        {
            var Q0;
            Q0=makeQuery(id+"F1.opExtrude","CAP_EDGE",EDGE,{"disambiguationData":[OSD([sQuery(id+"F0.wireOp",EDGE,"E1.bottom")])],"isStart":false});
            fillet(context, id + "F15", {"entities" : qUnion([Q0]), "radius" : 2 * mm, "tangentPropagation" : true, "allowEdgeOverflow" : false});
        }
        {
            var Q0;
            Q0=qCreatedBy(makeId("Top.planeOp"),FACE);
            var sketch = newSketch(context, id + "F16", { "sketchPlane" : qUnion([Q0])});
            skLineSegment(sketch, "E79.0", {"start": v(-80, 80) * mm, "end": v(80, 80) * mm});
            skArc(sketch, "E79.1", {"start": v(-80, 80) * mm, "mid": v(-87.07, 77.07) * mm, "end": v(-90, 70) * mm});
            skLineSegment(sketch, "E79.2", {"start": v(-90, -70) * mm, "end": v(-90, 70) * mm});
            skCircle(sketch, "E79.3", {"center": v(-60, 53.33) * mm, "radius": 4 * mm});
            skArc(sketch, "E79.4", {"start": v(52.38, 47.01) * mm, "mid": v(0, 53.33) * mm, "end": v(-52.38, 47.01) * mm});
            skArc(sketch, "E79.5", {"start": v(-52.38, 47.01) * mm, "mid": v(-57.87, 43.47) * mm, "end": v(-60, 37.3) * mm});
            skLineSegment(sketch, "E79.6", {"start": v(-60, 37.3) * mm, "end": v(-60, -37.3) * mm});
            skCircle(sketch, "E79.7", {"center": v(-60, -53.33) * mm, "radius": 4 * mm});
            skArc(sketch, "E79.8", {"start": v(-60, -37.3) * mm, "mid": v(-57.87, -43.47) * mm, "end": v(-52.38, -47.01) * mm});
            skArc(sketch, "E79.9", {"start": v(-90, -70) * mm, "mid": v(-87.07, -77.07) * mm, "end": v(-80, -80) * mm});
            skArc(sketch, "E79.10", {"start": v(-52.38, -47.01) * mm, "mid": v(0, -53.33) * mm, "end": v(52.38, -47.01) * mm});
            skLineSegment(sketch, "E79.11", {"start": v(-80, -80) * mm, "end": v(80, -80) * mm});
            skCircle(sketch, "E79.12", {"center": v(60, -53.33) * mm, "radius": 4 * mm});
            skArc(sketch, "E79.13", {"start": v(80, -80) * mm, "mid": v(87.07, -77.07) * mm, "end": v(90, -70) * mm});
            skLineSegment(sketch, "E79.14", {"start": v(90, -70) * mm, "end": v(90, 70) * mm});
            skArc(sketch, "E79.15", {"start": v(52.38, -47.01) * mm, "mid": v(57.87, -43.47) * mm, "end": v(60, -37.3) * mm});
            skLineSegment(sketch, "E79.16", {"start": v(60, 37.3) * mm, "end": v(60, -37.3) * mm});
            skArc(sketch, "E79.17", {"start": v(60, 37.3) * mm, "mid": v(57.87, 43.47) * mm, "end": v(52.38, 47.01) * mm});
            skCircle(sketch, "E79.18", {"center": v(60, 53.33) * mm, "radius": 4 * mm});
            skArc(sketch, "E79.19", {"start": v(90, 70) * mm, "mid": v(87.07, 77.07) * mm, "end": v(80, 80) * mm});
            skLineSegment(sketch, "E80", {"start": v(0, 80) * mm, "end": v(0, 110) * mm, "construction": true});
            skPoint(sketch, "E80.endSnap0", {"position": v(0, 80) * mm});
            skCircle(sketch, "E81", {"center": v(0, 110) * mm, "radius": 6 * mm});
            skArc(sketch, "E82", {"start": v(15, 110) * mm, "mid": v(0, 125.1) * mm, "end": v(-15, 110) * mm});
            skLineSegment(sketch, "E83", {"start": v(-15, 110) * mm, "end": v(-14.92, 98) * mm});
            skLineSegment(sketch, "E84", {"start": v(15, 110) * mm, "end": v(15, 98) * mm});
            skLineSegment(sketch, "E85", {"start": v(-32.92, 80) * mm, "end": v(-14.92, 98) * mm});
            skLineSegment(sketch, "E86", {"start": v(33, 80) * mm, "end": v(15, 98) * mm});
            skLineSegment(sketch, "E87", {"start": v(-32.92, 80) * mm, "end": v(33, 80) * mm});
            skLineSegment(sketch, "E88", {"start": v(90, 0) * mm, "end": v(-90, 0) * mm, "construction": true});
            skLineSegment(sketch, "E89.MirrorCS", {"start": v(-32.92, -80) * mm, "end": v(33, -80) * mm});
            skCircle(sketch, "E90.MirrorC", {"center": v(0, -110) * mm, "radius": 6 * mm});
            skLineSegment(sketch, "E91.MirrorCS", {"start": v(-15, -110) * mm, "end": v(-14.92, -98) * mm});
            skArc(sketch, "E92.MirrorCS", {"start": v(52.38, 47.01) * mm, "mid": v(57.87, 43.47) * mm, "end": v(60, 37.3) * mm});
            skLineSegment(sketch, "E93.MirrorCS", {"start": v(-32.92, -80) * mm, "end": v(-14.92, -98) * mm});
            skArc(sketch, "E94.MirrorCS", {"start": v(-90, 70) * mm, "mid": v(-87.07, 77.07) * mm, "end": v(-80, 80) * mm});
            skLineSegment(sketch, "E95.MirrorCS", {"start": v(-90, 70) * mm, "end": v(-90, -70) * mm});
            skArc(sketch, "E96.MirrorCS", {"start": v(-80, -80) * mm, "mid": v(-87.07, -77.07) * mm, "end": v(-90, -70) * mm});
            skLineSegment(sketch, "E97.MirrorCS", {"start": v(33, -80) * mm, "end": v(15, -98) * mm});
            skArc(sketch, "E98.MirrorCS", {"start": v(52.38, -47.01) * mm, "mid": v(0, -53.33) * mm, "end": v(-52.38, -47.01) * mm});
            skArc(sketch, "E99.MirrorCS", {"start": v(60, -37.3) * mm, "mid": v(57.87, -43.47) * mm, "end": v(52.38, -47.01) * mm});
            skArc(sketch, "E100.MirrorCS", {"start": v(-52.38, -47.01) * mm, "mid": v(-57.87, -43.47) * mm, "end": v(-60, -37.3) * mm});
            skLineSegment(sketch, "E101.MirrorCS", {"start": v(0, -80) * mm, "end": v(0, -110) * mm, "construction": true});
            skLineSegment(sketch, "E102.MirrorCS", {"start": v(-60, -37.3) * mm, "end": v(-60, 37.3) * mm});
            skArc(sketch, "E103.MirrorCS", {"start": v(15, -110) * mm, "mid": v(0, -125.1) * mm, "end": v(-15, -110) * mm});
            skLineSegment(sketch, "E104.MirrorCS", {"start": v(90, 70) * mm, "end": v(90, -70) * mm});
            skLineSegment(sketch, "E105.MirrorCS", {"start": v(15, -110) * mm, "end": v(15, -98) * mm});
            skLineSegment(sketch, "E106.MirrorCS", {"start": v(60, -37.3) * mm, "end": v(60, 37.3) * mm});
            skPoint(sketch, "E107.MirrorP", {"position": v(0, -80) * mm});
            skArc(sketch, "E108.MirrorCS", {"start": v(-52.38, 47.01) * mm, "mid": v(0, 53.33) * mm, "end": v(52.38, 47.01) * mm});
            skArc(sketch, "E109.MirrorCS", {"start": v(80, 80) * mm, "mid": v(87.07, 77.07) * mm, "end": v(90, 70) * mm});
            skArc(sketch, "E110.MirrorCS", {"start": v(-60, 37.3) * mm, "mid": v(-57.87, 43.47) * mm, "end": v(-52.38, 47.01) * mm});
            skArc(sketch, "E111.MirrorCS", {"start": v(90, -70) * mm, "mid": v(87.07, -77.07) * mm, "end": v(80, -80) * mm});
            skSolve(sketch);
        }
        {
            var Q0;
            Q0 = qSketchRegion(id + "F16", true);
            extrude(context, id + "F17", {"entities" : qUnion([Q0]), "operationType" : NewBodyOperationType.ADD, "endBound" : BoundingType.SYMMETRIC, "depth" : 6 * mm});
        }
    });
